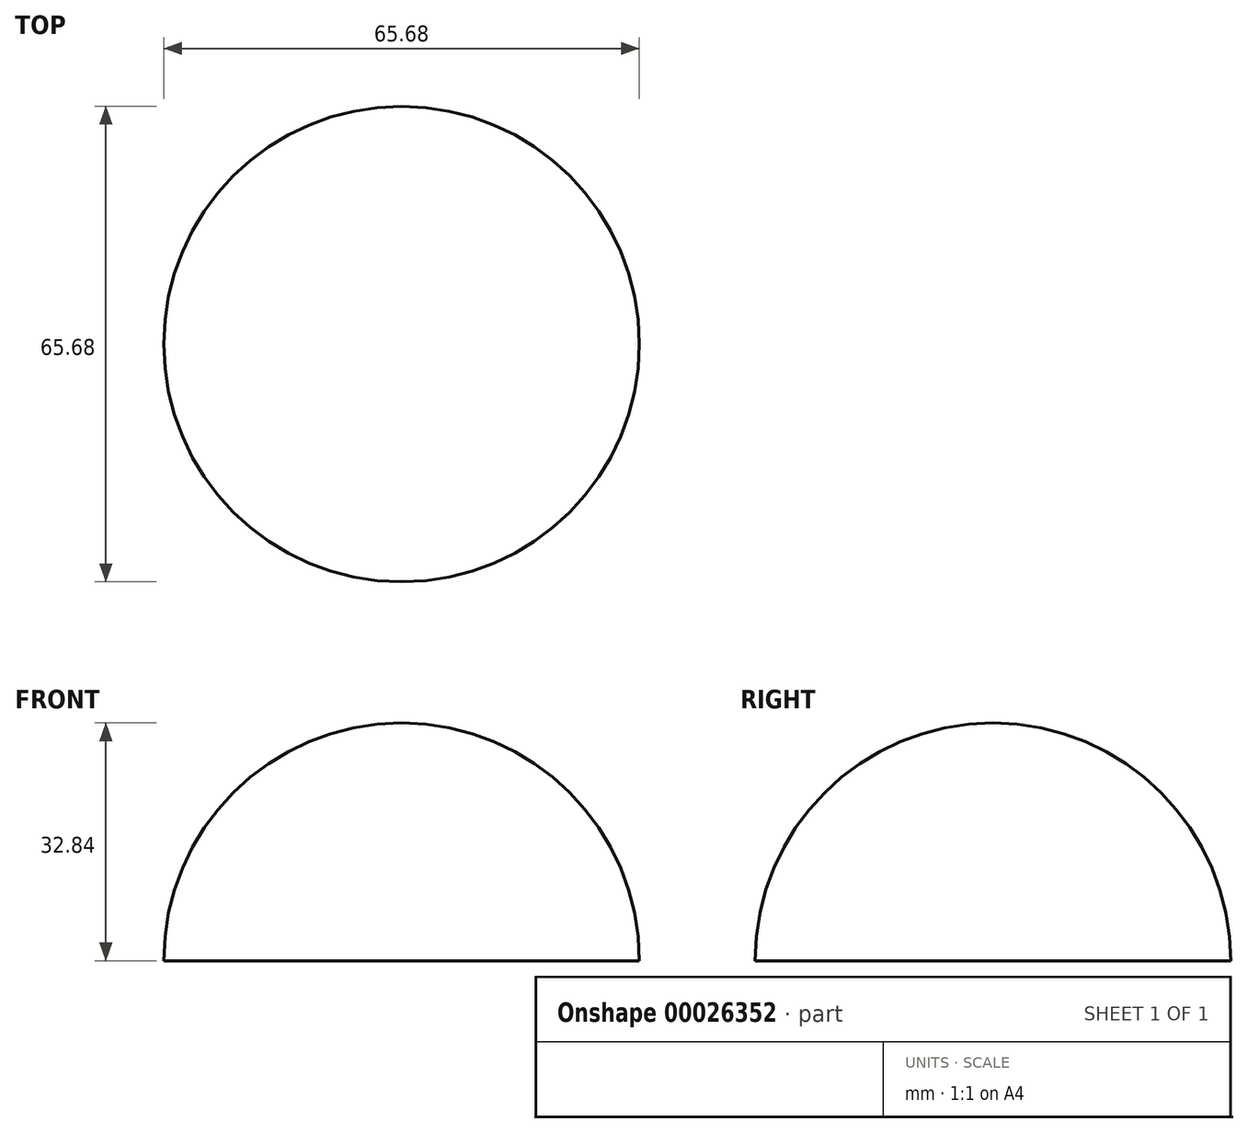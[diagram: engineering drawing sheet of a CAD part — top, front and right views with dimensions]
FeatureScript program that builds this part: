
annotation { "Feature Type Name" : "Feature", "Feature Type Description" : "" }
export const myFeature = defineFeature(function(context is Context, id is Id, definition is map)
    precondition{}
    {
        {
            var Q0;
            Q0=qCreatedBy(makeId("Top.planeOp"),FACE);
            var sketch = newSketch(context, id + "F0", { "sketchPlane" : qUnion([Q0])});
            skCircle(sketch, "E0", {"center": v(0, 0) * mm, "radius": 32.84 * mm});
            skLineSegment(sketch, "E1", {"start": v(0, 32.84) * mm, "end": v(0, -32.84) * mm});
            skSolve(sketch);
        }
        {
            var Q0;
            {var subQ0=sQuery(id+"F0.wireOp",EDGE,"E1");Q0=makeQuery(id+"F0.imprint","IMPRINT",FACE,{"disambiguationData":[TD([[makeQuery(id+"F0.imprint","IMPRINT",EDGE,{"derivedFrom":subQ0}),-1.0]])]});}
            var Q1;
            Q1=sQuery(id+"F0.wireOp",EDGE,"E1");
            revolve(context, id + "F1", {"entities" : qUnion([Q0]), "axis" : qUnion([Q1]), "revolveType" : RevolveType.ONE_DIRECTION, "oppositeDirection" : true, "angle" : 180 * degree});
        }
    });
